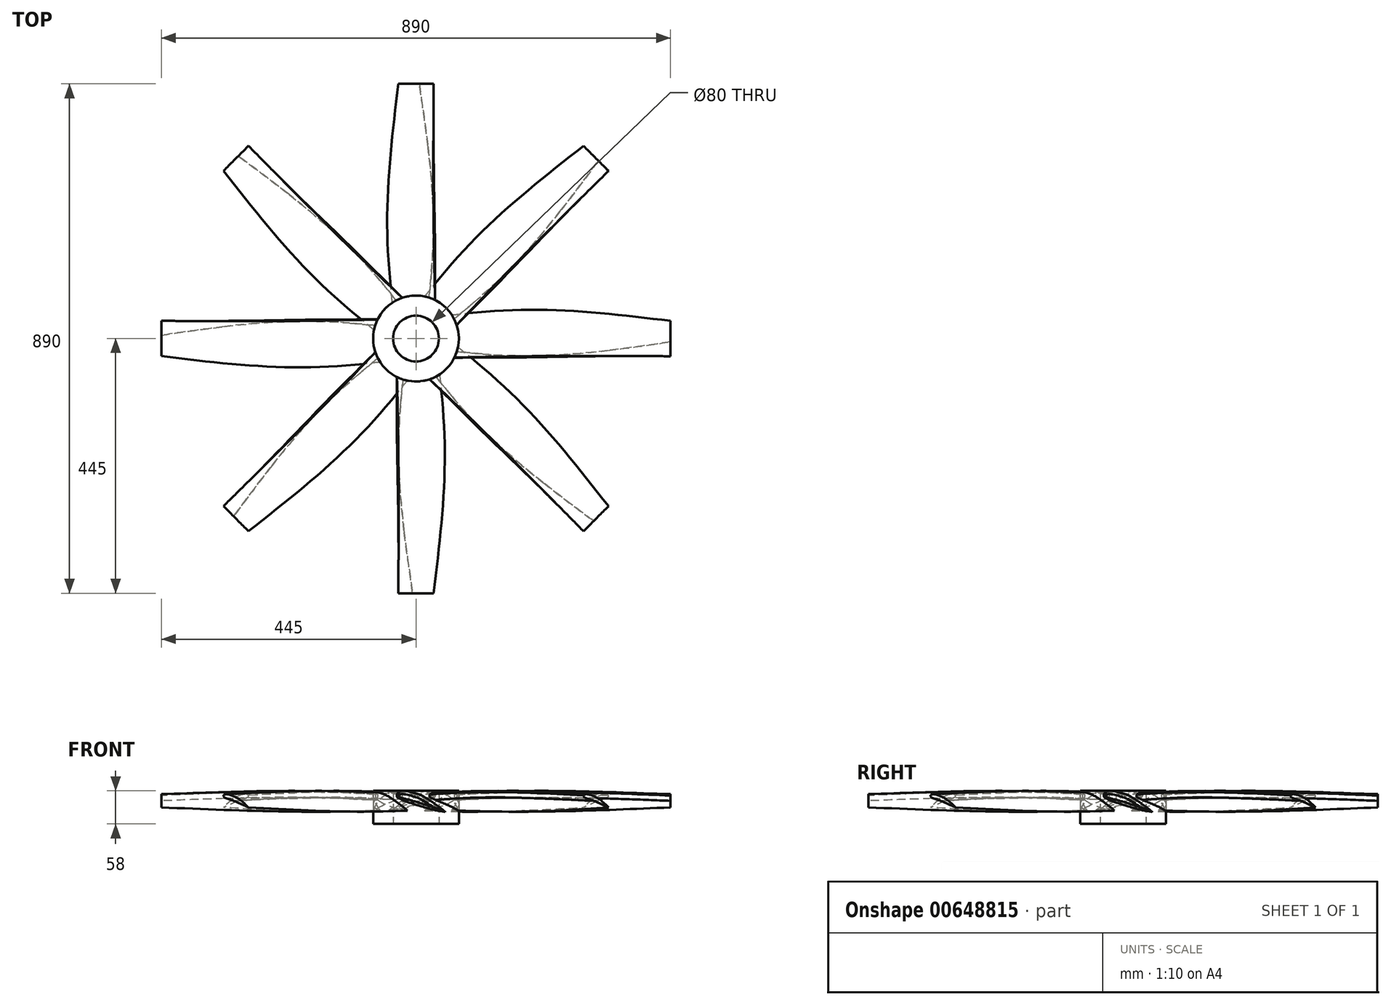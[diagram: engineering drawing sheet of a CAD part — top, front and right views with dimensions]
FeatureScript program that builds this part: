
annotation { "Feature Type Name" : "Feature", "Feature Type Description" : "" }
export const myFeature = defineFeature(function(context is Context, id is Id, definition is map)
    precondition{}
    {
        {
            var Q0;
            Q0=qCreatedBy(makeId("Front.planeOp"),FACE);
            var sketch = newSketch(context, id + "F0", { "sketchPlane" : qUnion([Q0])});
            skFitSpline(sketch, "E0", {"points": [v(-33.84, 21.14) * mm, v(-29.49, 24.4) * mm, v(6.99, 18.05) * mm, v(39.47, -5.17) * mm, v(39.28, -5.17) * mm], "startDerivative": vector(19.8, 24.1) * mm, "endDerivative": vector(-9.16, 2.3) * mm});
            skFitSpline(sketch, "E1", {"points": [v(39.47, -5.17) * mm, v(-31.37, 15.8) * mm, v(-33.32, 17.09) * mm, v(-33.84, 21.14) * mm], "startDerivative": vector(-142.45, 33.16) * mm, "endDerivative": vector(3.68, 29.23) * mm});
            skSolve(sketch);
        }
        {
            var Q0;
            Q0=qCreatedBy(makeId("Front.planeOp"),FACE);
            cPlane(context, id + "F1", {"entities" : qUnion([Q0]), "cplaneType" : CPlaneType.OFFSET, "offset" : 125 * mm, "width" : 150 * mm, "height" : 150 * mm});
        }
        {
            var Q0;
            Q0=qCreatedBy(id+"F1.planeOp",FACE);
            var sketch = newSketch(context, id + "F2", { "sketchPlane" : qUnion([Q0])});
            skFitSpline(sketch, "E2", {"points": [v(-35.11, 23.68) * mm, v(-24.95, 28.22) * mm, v(2.45, 23.32) * mm, v(25.68, 10.8) * mm, v(44.9, -3.36) * mm, v(49.79, -7.53) * mm], "startDerivative": vector(75.82, 46.97) * mm, "endDerivative": vector(34.05, -30.53) * mm});
            skFitSpline(sketch, "E3", {"points": [v(-31.13, 26.15) * mm, v(-32.97, 23.58) * mm, v(-33.06, 21.68) * mm, v(-30.12, 16.7) * mm], "startDerivative": vector(-8.93, -6.19) * mm, "endDerivative": vector(12.7, -11.5) * mm});
            skFitSpline(sketch, "E4.trimOffspring", {"points": [v(-34.94, 23.01) * mm, v(-31, 17.33) * mm, v(-19.9, 11.5) * mm, v(14.78, 0) * mm, v(49.87, -7.54) * mm], "startDerivative": vector(11.43, -58.64) * mm, "endDerivative": vector(114.26, -12.01) * mm});
            skPoint(sketch, "E5.3.internal.orphan", {"position": v(14.79, 0) * mm});
            skSolve(sketch);
        }
        {
            var Q0;
            Q0=qCreatedBy(makeId("Front.planeOp"),FACE);
            cPlane(context, id + "F3", {"entities" : qUnion([Q0]), "cplaneType" : CPlaneType.OFFSET, "offset" : 400 * mm, "width" : 150 * mm, "height" : 150 * mm});
        }
        {
            var Q0;
            Q0=qCreatedBy(id+"F3.planeOp",FACE);
            var sketch = newSketch(context, id + "F4", { "sketchPlane" : qUnion([Q0])});
            skFitSpline(sketch, "E6", {"points": [v(-30.91, 20.61) * mm, v(-28.33, 22.39) * mm, v(-19.92, 22.87) * mm, v(-5.37, 19.48) * mm, v(9.66, 13.5) * mm, v(30.83, 0) * mm], "startDerivative": vector(21.25, 19.84) * mm, "endDerivative": vector(77, -53.08) * mm});
            skFitSpline(sketch, "E7", {"points": [v(-30.91, 20.61) * mm, v(-29.3, 18.03) * mm, v(-23.32, 15.76) * mm, v(-6.34, 11.56) * mm, v(18.87, 3.8) * mm, v(30.83, 0) * mm], "startDerivative": vector(11.54, -27.53) * mm, "endDerivative": vector(51.48, -16.24) * mm});
            skSolve(sketch);
        }
        {
            var Q0;
            {var subQ0=sQuery(id+"F0.wireOp",EDGE,"E1");Q0=makeQuery(id+"F0.imprint","IMPRINT",FACE,{"disambiguationData":[TD([[makeQuery(id+"F0.imprint","IMPRINT",EDGE,{"derivedFrom":subQ0}),-1.0]])]});}
            var Q1;
            {var subQ0=sQuery(id+"F2.wireOp",EDGE,"E2");Q1=makeQuery(id+"F2.imprint","IMPRINT",FACE,{"disambiguationData":[TD([[makeQuery(id+"F2.imprint","IMPRINT",EDGE,{"derivedFrom":subQ0}),-1.0]])]});}
            var Q2;
            Q2=makeQuery(id+"F4.imprint","IMPRINT",FACE,{"disambiguationData":[TD([[makeQuery(id+"F4.imprint","IMPRINT",EDGE,{"derivedFrom":sQuery(id+"F4.wireOp",EDGE,"E6")}),-1.0]])]});
            loft(context, id + "F5", {"sheetProfilesArray" : [{ "sheetProfileEntities" : qUnion([Q0]) }, { "sheetProfileEntities" : qUnion([Q1]) }, { "sheetProfileEntities" : qUnion([Q2]) }]});
        }
        {
            var Q0;
            Q0=makeQuery(id+"F5.opLoft","SWEPT_EDGE",EDGE,{"disambiguationData":[OSD([sQuery(id+"F0.wireOp",EDGE,"E1"),sQuery(id+"F2.wireOp",EDGE,"E2"),sQuery(id+"F2.wireOp",EDGE,"E3"),sQuery(id+"F2.wireOp",EDGE,"E4.trimOffspring")])]});
            var Q1;
            Q1=makeQuery(id+"F5.opLoft","SWEPT_EDGE",EDGE,{"disambiguationData":[OSD([sQuery(id+"F2.wireOp",EDGE,"E2"),sQuery(id+"F2.wireOp",EDGE,"E3"),sQuery(id+"F2.wireOp",EDGE,"E4.trimOffspring"),sQuery(id+"F4.wireOp",EDGE,"E7")])]});
            fillet(context, id + "F6", {"entities" : qUnion([Q0, Q1]), "radius" : 2 * mm, "tangentPropagation" : true, "allowEdgeOverflow" : false});
        }
        {
            var Q0;
            {var subQ0=sQuery(id+"F0.wireOp",EDGE,"E1");Q0=makeQuery(id+"F5.opLoft","SWEPT_BODY",BODY,{"disambiguationData":[OSD([makeQuery(id+"F0.imprint","IMPRINT",FACE,{"disambiguationData":[TD([[makeQuery(id+"F0.imprint","IMPRINT",EDGE,{"derivedFrom":subQ0}),-1.0]])]}),sQuery(id+"F2.wireOp",EDGE,"E3"),makeQuery(id+"F4.imprint","IMPRINT",FACE,{"disambiguationData":[TD([[makeQuery(id+"F4.imprint","IMPRINT",EDGE,{"derivedFrom":sQuery(id+"F4.wireOp",EDGE,"E6")}),-1.0]])]})])]});}
            transform(context, id + "F7", {"entities" : qUnion([Q0]), "transformType" : TransformType.TRANSLATION_3D, "dx" : 0 * mm, "dy" : -45 * mm, "dz" : 0 * mm, "makeCopy" : false});
        }
        {
            var Q0;
            Q0=qCreatedBy(makeId("Top.planeOp"),FACE);
            var sketch = newSketch(context, id + "F8", { "sketchPlane" : qUnion([Q0])});
            skCircle(sketch, "E8", {"center": v(0, 0) * mm, "radius": 75 * mm});
            skCircle(sketch, "E9", {"center": v(0, 0) * mm, "radius": 40 * mm});
            skSolve(sketch);
        }
        {
            var Q0;
            Q0=makeQuery(id+"F8.imprint","IMPRINT",FACE,{"disambiguationData":[TD([[makeQuery(id+"F8.imprint","IMPRINT",EDGE,{"derivedFrom":sQuery(id+"F8.wireOp",EDGE,"E8")}),1.0]])]});
            extrude(context, id + "F9", {"entities" : qUnion([Q0]), "operationType" : NewBodyOperationType.REMOVE, "endBound" : BoundingType.SYMMETRIC, "depth" : 98 * mm, "offsetDistance" : 25 * mm});
        }
        {
            var Q0;
            {var subQ0=sQuery(id+"F0.wireOp",EDGE,"E1");Q0=makeQuery(id+"F5.opLoft","SWEPT_BODY",BODY,{"disambiguationData":[OSD([makeQuery(id+"F0.imprint","IMPRINT",FACE,{"disambiguationData":[TD([[makeQuery(id+"F0.imprint","IMPRINT",EDGE,{"derivedFrom":subQ0}),-1.0]])]}),sQuery(id+"F2.wireOp",EDGE,"E3"),makeQuery(id+"F4.imprint","IMPRINT",FACE,{"disambiguationData":[TD([[makeQuery(id+"F4.imprint","IMPRINT",EDGE,{"derivedFrom":sQuery(id+"F4.wireOp",EDGE,"E6")}),-1.0]])]})])]});}
            var Q1;
            Q1=sQuery(id+"F8.wireOp",EDGE,"E8");
            circularPattern(context, id + "F10", {"entities" : qUnion([Q0]), "axis" : qUnion([Q1]), "angle" : 360 * degree, "instanceCount" : 8, "equalSpace" : true});
        }
        {
            var Q0;
            Q0=makeQuery(id+"F8.imprint","IMPRINT",FACE,{"disambiguationData":[TD([[makeQuery(id+"F8.imprint","IMPRINT",EDGE,{"derivedFrom":sQuery(id+"F8.wireOp",EDGE,"E8")}),1.0]])]});
            extrude(context, id + "F11", {"entities" : qUnion([Q0]), "endBound" : BoundingType.SYMMETRIC, "depth" : 58 * mm, "offsetDistance" : 25 * mm});
        }
    });
